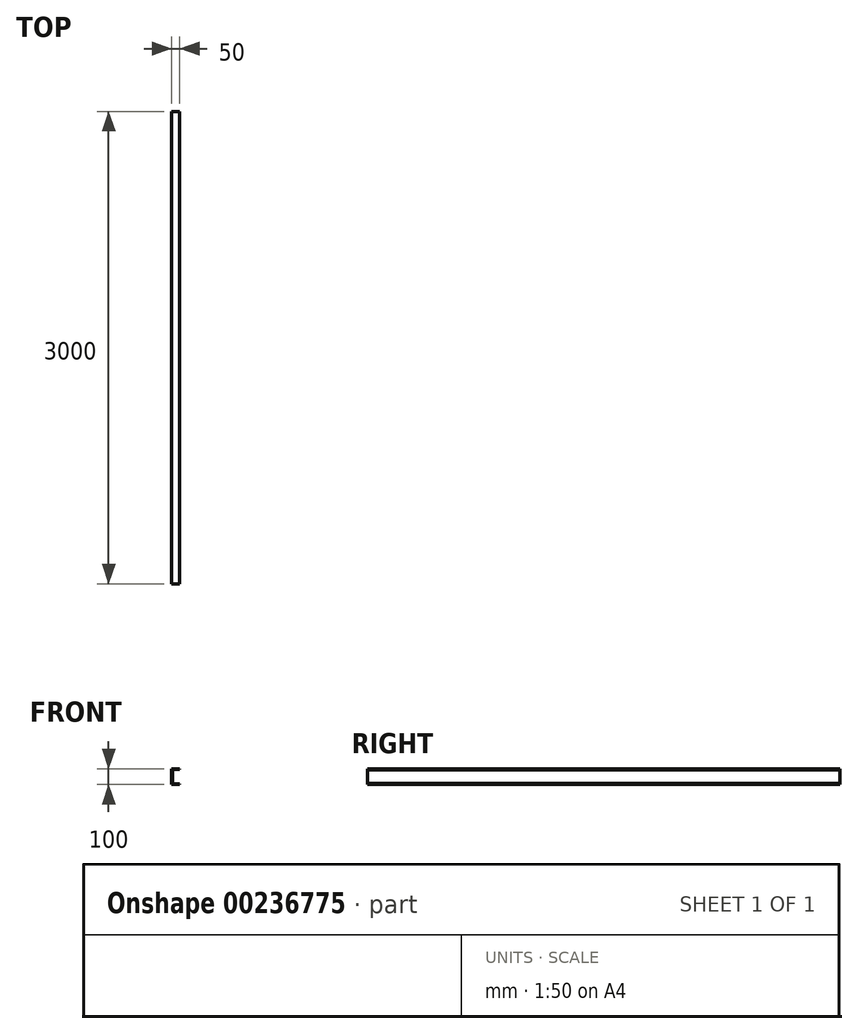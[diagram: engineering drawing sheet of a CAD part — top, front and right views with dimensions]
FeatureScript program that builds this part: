
annotation { "Feature Type Name" : "Feature", "Feature Type Description" : "" }
export const myFeature = defineFeature(function(context is Context, id is Id, definition is map)
    precondition{}
    {
        {
            var Q0;
            Q0=qCreatedBy(makeId("Front.planeOp"),FACE);
            var sketch = newSketch(context, id + "F0", { "sketchPlane" : qUnion([Q0])});
            skLineSegment(sketch, "E0.bottom", {"start": v(0, 0) * mm, "end": v(50, 0) * mm});
            skLineSegment(sketch, "E0.top", {"start": v(0, 100) * mm, "end": v(50, 100) * mm});
            skLineSegment(sketch, "E0.left", {"start": v(0, 0) * mm, "end": v(0, 100) * mm});
            skLineSegment(sketch, "E0.right", {"start": v(50, 0) * mm, "end": v(50, 5) * mm});
            skLineSegment(sketch, "E1.left", {"start": v(4.68, 71.03) * mm, "end": v(4.68, 71.03) * mm});
            skLineSegment(sketch, "E1.right", {"start": v(12.2, 71.03) * mm, "end": v(12.2, 71.03) * mm});
            skLineSegment(sketch, "E2", {"start": v(6, 8.46) * mm, "end": v(50, 5) * mm});
            skLineSegment(sketch, "E3", {"start": v(6, 8.46) * mm, "end": v(6, 93.46) * mm});
            skLineSegment(sketch, "E4", {"start": v(6, 93.46) * mm, "end": v(50, 95) * mm});
            skLineSegment(sketch, "E5.trimOffspring", {"start": v(50, 95) * mm, "end": v(50, 100) * mm});
            skSolve(sketch);
        }
        {
            var Q0;
            Q0=makeQuery(id+"F0.imprint","IMPRINT",FACE,{"disambiguationData":[TD([[makeQuery(id+"F0.imprint","IMPRINT",EDGE,{"derivedFrom":sQuery(id+"F0.wireOp",EDGE,"E0.bottom")}),1.0]])]});
            extrude(context, id + "F1", {"entities" : qUnion([Q0]), "depth" : 3000 * mm, "offsetDistance" : 25 * mm});
        }
    });
